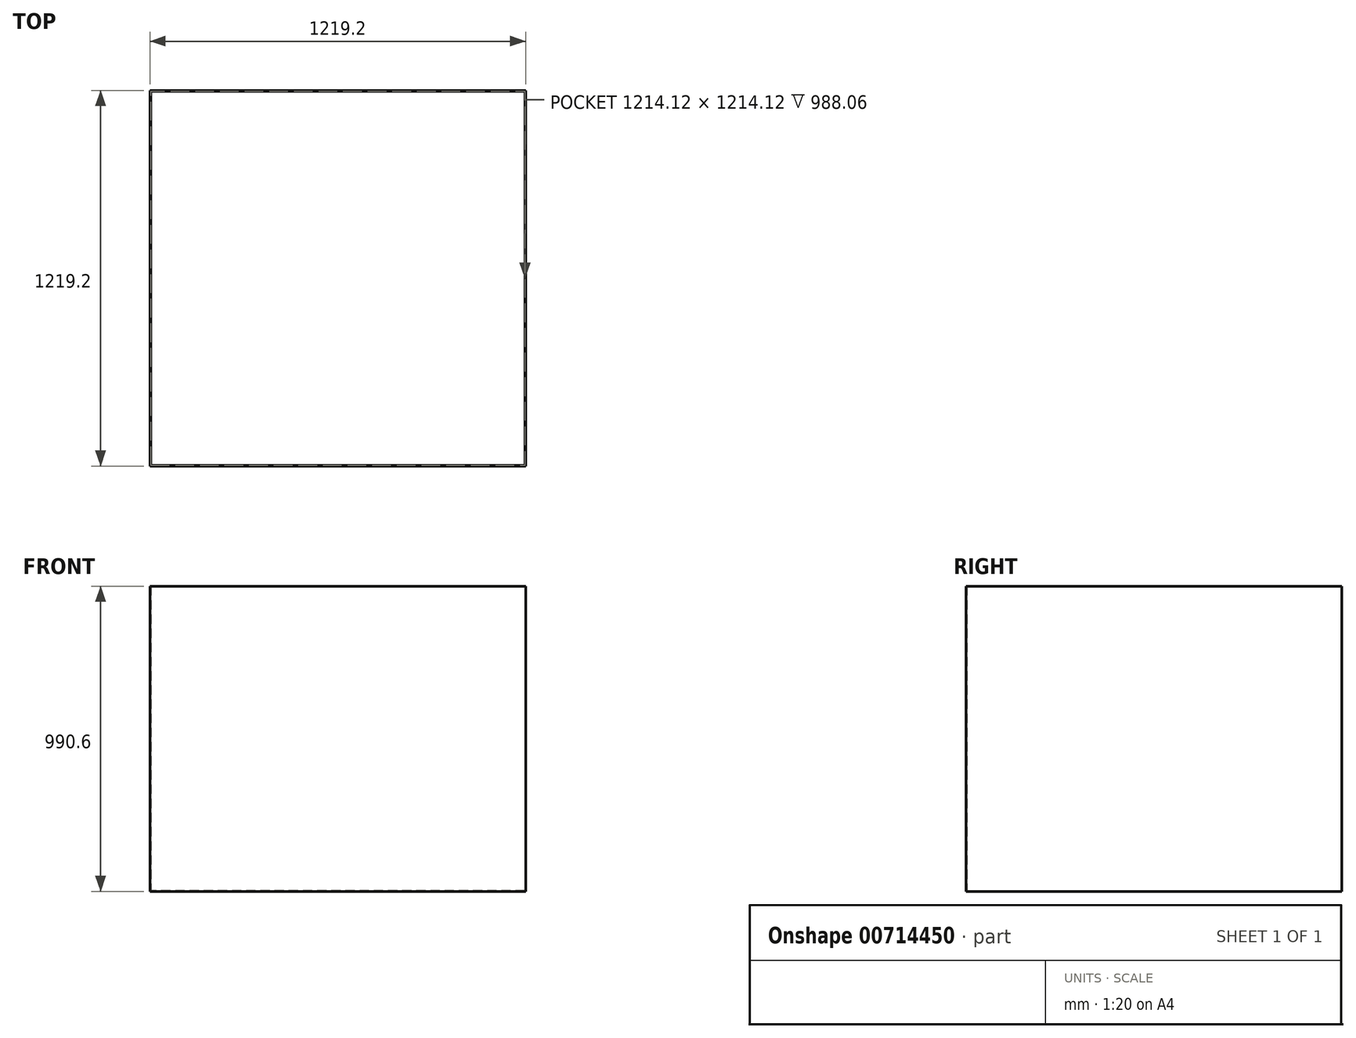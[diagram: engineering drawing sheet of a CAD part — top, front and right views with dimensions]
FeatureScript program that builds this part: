
annotation { "Feature Type Name" : "Feature", "Feature Type Description" : "" }
export const myFeature = defineFeature(function(context is Context, id is Id, definition is map)
    precondition{}
    {
        {
            var Q0;
            Q0=qCreatedBy(makeId("Top.planeOp"),FACE);
            var sketch = newSketch(context, id + "F0", { "sketchPlane" : qUnion([Q0])});
            skLineSegment(sketch, "E0.bottom", {"start": v(609.6, -609.6) * mm, "end": v(-609.6, -609.6) * mm});
            skLineSegment(sketch, "E0.top", {"start": v(609.6, 609.6) * mm, "end": v(-609.6, 609.6) * mm});
            skLineSegment(sketch, "E0.left", {"start": v(609.6, -609.6) * mm, "end": v(609.6, 609.6) * mm});
            skLineSegment(sketch, "E0.right", {"start": v(-609.6, -609.6) * mm, "end": v(-609.6, 609.6) * mm});
            skPoint(sketch, "E0.middle", {"position": v(0, 0) * mm});
            skSolve(sketch);
        }
        {
            var Q0;
            Q0=makeQuery(id+"F0.imprint","IMPRINT",FACE,{"disambiguationData":[TD([[makeQuery(id+"F0.imprint","IMPRINT",EDGE,{"derivedFrom":sQuery(id+"F0.wireOp",EDGE,"E0.bottom")}),-1.0]])]});
            extrude(context, id + "F1", {"entities" : qUnion([Q0]), "depth" : 990.6 * mm, "offsetDistance" : 25.4 * mm});
        }
        {
            var Q0;
            Q0=makeQuery(id+"F1.opExtrude","CAP_FACE",FACE,{"disambiguationData":[OSD([sQuery(id+"F0.wireOp",EDGE,"E0.bottom"),sQuery(id+"F0.wireOp",EDGE,"E0.top"),sQuery(id+"F0.wireOp",EDGE,"E0.left"),sQuery(id+"F0.wireOp",EDGE,"E0.right")])],"isStart":false});
            shell(context, id + "F2", {"entities" : qUnion([Q0]), "thickness" : 2.54 * mm});
        }
        {
            var Q0;
            Q0=makeQuery(id+"F1.opExtrude","SWEPT_FACE",FACE,{"disambiguationData":[OSD([sQuery(id+"F0.wireOp",EDGE,"E0.bottom")])]});
            var sketch = newSketch(context, id + "F3", { "sketchPlane" : qUnion([Q0])});
            skLineSegment(sketch, "E1.bottom", {"start": v(-609.6, 0) * mm, "end": v(-381, 0) * mm});
            skLineSegment(sketch, "E1.top", {"start": v(-609.6, -127) * mm, "end": v(-381, -127) * mm});
            skLineSegment(sketch, "E1.left", {"start": v(-609.6, 0) * mm, "end": v(-609.6, -127) * mm});
            skLineSegment(sketch, "E1.right", {"start": v(-381, 0) * mm, "end": v(-381, -127) * mm});
            skLineSegment(sketch, "E2.bottom", {"start": v(609.6, 0) * mm, "end": v(381, 0) * mm});
            skLineSegment(sketch, "E2.top", {"start": v(609.6, -127) * mm, "end": v(381, -127) * mm});
            skLineSegment(sketch, "E2.left", {"start": v(609.6, 0) * mm, "end": v(609.6, -127) * mm});
            skLineSegment(sketch, "E2.right", {"start": v(381, 0) * mm, "end": v(381, -127) * mm});
            skSolve(sketch);
        }
        {
            var Q0;
            Q0=makeQuery(id+"F3.imprint","IMPRINT",FACE,{"disambiguationData":[TD([[makeQuery(id+"F3.imprint","IMPRINT",EDGE,{"derivedFrom":sQuery(id+"F3.wireOp",EDGE,"E1.bottom")}),1.0]])]});
            var Q1;
            Q1=makeQuery(id+"F3.imprint","IMPRINT",FACE,{"disambiguationData":[TD([[makeQuery(id+"F3.imprint","IMPRINT",EDGE,{"derivedFrom":sQuery(id+"F3.wireOp",EDGE,"E2.bottom")}),1.0]])]});
            var Q2;
            Q2=sQuery(id+"F3.wireOp",EDGE,"E1.left");
            var Q3;
            Q3=sQuery(id+"F3.wireOp",EDGE,"E1.top");
            var Q4;
            Q4=sQuery(id+"F3.wireOp",EDGE,"E1.right");
            var Q5;
            Q5=sQuery(id+"F3.wireOp",EDGE,"E2.right");
            var Q6;
            Q6=sQuery(id+"F3.wireOp",EDGE,"E2.top");
            var Q7;
            Q7=sQuery(id+"F3.wireOp",EDGE,"E2.left");
            extrude(context, id + "F4", {"entities" : qUnion([Q0, Q1]), "bodyType" : ToolBodyType.SURFACE, "operationType" : NewBodyOperationType.ADD, "surfaceEntities" : qUnion([Q2, Q3, Q4, Q5, Q6, Q7]), "oppositeDirection" : true, "depth" : 1219.2 * mm, "offsetDistance" : 25.4 * mm});
        }
    });
